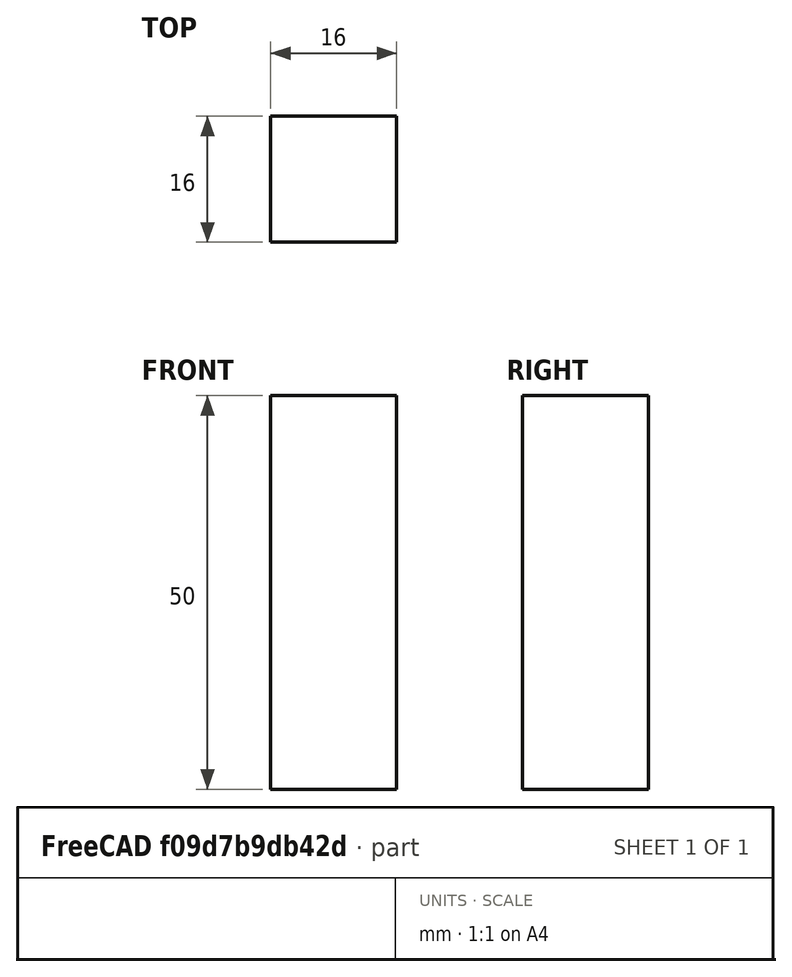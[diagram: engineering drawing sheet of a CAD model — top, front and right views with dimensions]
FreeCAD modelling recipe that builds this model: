
FCSTD DOCUMENT  (FreeCAD 0.15R4671 (Git))
Label: Square Bar 16 EN10059 S235JR
License: All rights reserved
LicenseURL: http://en.wikipedia.org/wiki/All_rights_reserved
objects: Sketcher::SketchObject×1, Part::Extrusion×1
note: 2 computed .brp shape members not serialized (recipe doc carries the construction recipe); baked Part::Feature solids carry a one-line shape summary decoded from their .brp

FEATURE [Sketcher::SketchObject] Sketch
  sketch-geometry (4):
    g0: LineSegment StartX=-8 StartY=-8 StartZ=0 EndX=8 EndY=-8 EndZ=0
    g1: LineSegment StartX=8 StartY=-8 StartZ=0 EndX=8 EndY=8 EndZ=0
    g2: LineSegment StartX=8 StartY=8 StartZ=0 EndX=-8 EndY=8 EndZ=0
    g3: LineSegment StartX=-8 StartY=8 StartZ=0 EndX=-8 EndY=-8 EndZ=0
  constraints (12):
    c: Coincident(g0,g1)
    c: Coincident(g1,g2)
    c: Coincident(g2,g3)
    c: Coincident(g3,g0)
    c: Horizontal(g0)
    c: Horizontal(g2)
    c: Vertical(g1)
    c: Vertical(g3)
    c: Symmetric(g1,g0,g-1)
    c: Symmetric(g2,g1,g-2)
    c: Equal(g1,g2)
    c: DistanceY(g1) = 16
FEATURE [Part::Extrusion] Extrude  label="Square Bar 16 EN10059 S235JR"
  Base = -> Sketch
  Dir = (0,0,50)
  Solid = true
